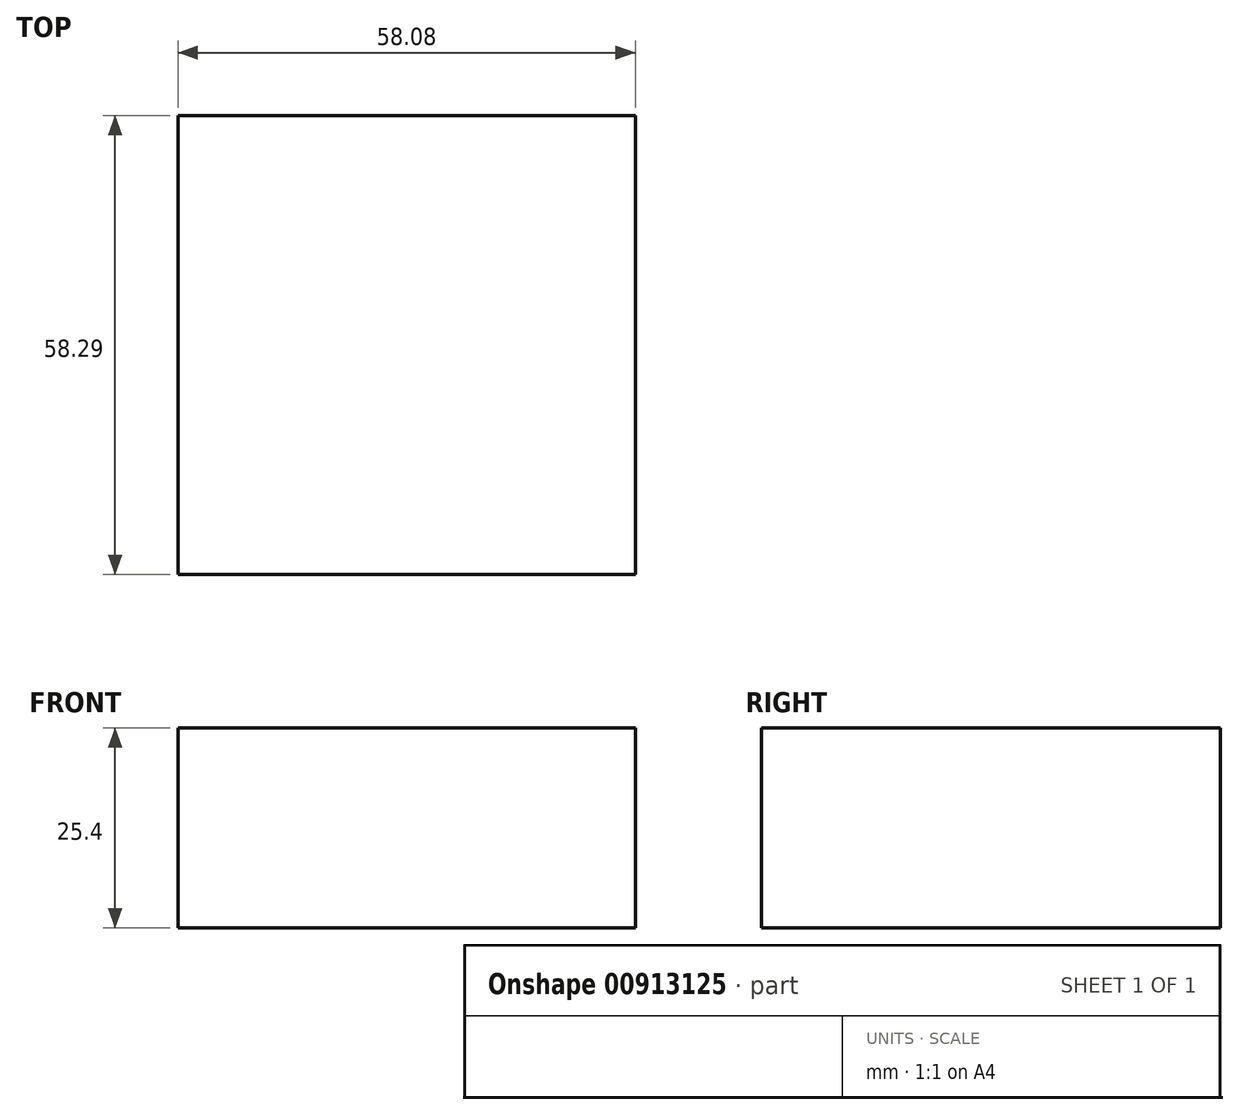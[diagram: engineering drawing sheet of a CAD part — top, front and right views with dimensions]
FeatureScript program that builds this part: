
annotation { "Feature Type Name" : "Feature", "Feature Type Description" : "" }
export const myFeature = defineFeature(function(context is Context, id is Id, definition is map)
    precondition{}
    {
        {
            var Q0;
            Q0=qCreatedBy(makeId("Top.planeOp"),FACE);
            var sketch = newSketch(context, id + "F0", { "sketchPlane" : qUnion([Q0])});
            skLineSegment(sketch, "E0.bottom", {"start": v(0, 0) * mm, "end": v(58.08, 0) * mm});
            skLineSegment(sketch, "E0.top", {"start": v(0, 58.29) * mm, "end": v(58.08, 58.29) * mm});
            skLineSegment(sketch, "E0.left", {"start": v(0, 0) * mm, "end": v(0, 58.29) * mm});
            skLineSegment(sketch, "E0.right", {"start": v(58.08, 0) * mm, "end": v(58.08, 58.29) * mm});
            skSolve(sketch);
        }
        {
            var Q0;
            Q0 = qSketchRegion(id + "F0", true);
            extrude(context, id + "F1", {"entities" : qUnion([Q0]), "depth" : 25.4 * mm, "offsetDistance" : 25.4 * mm});
        }
    });
